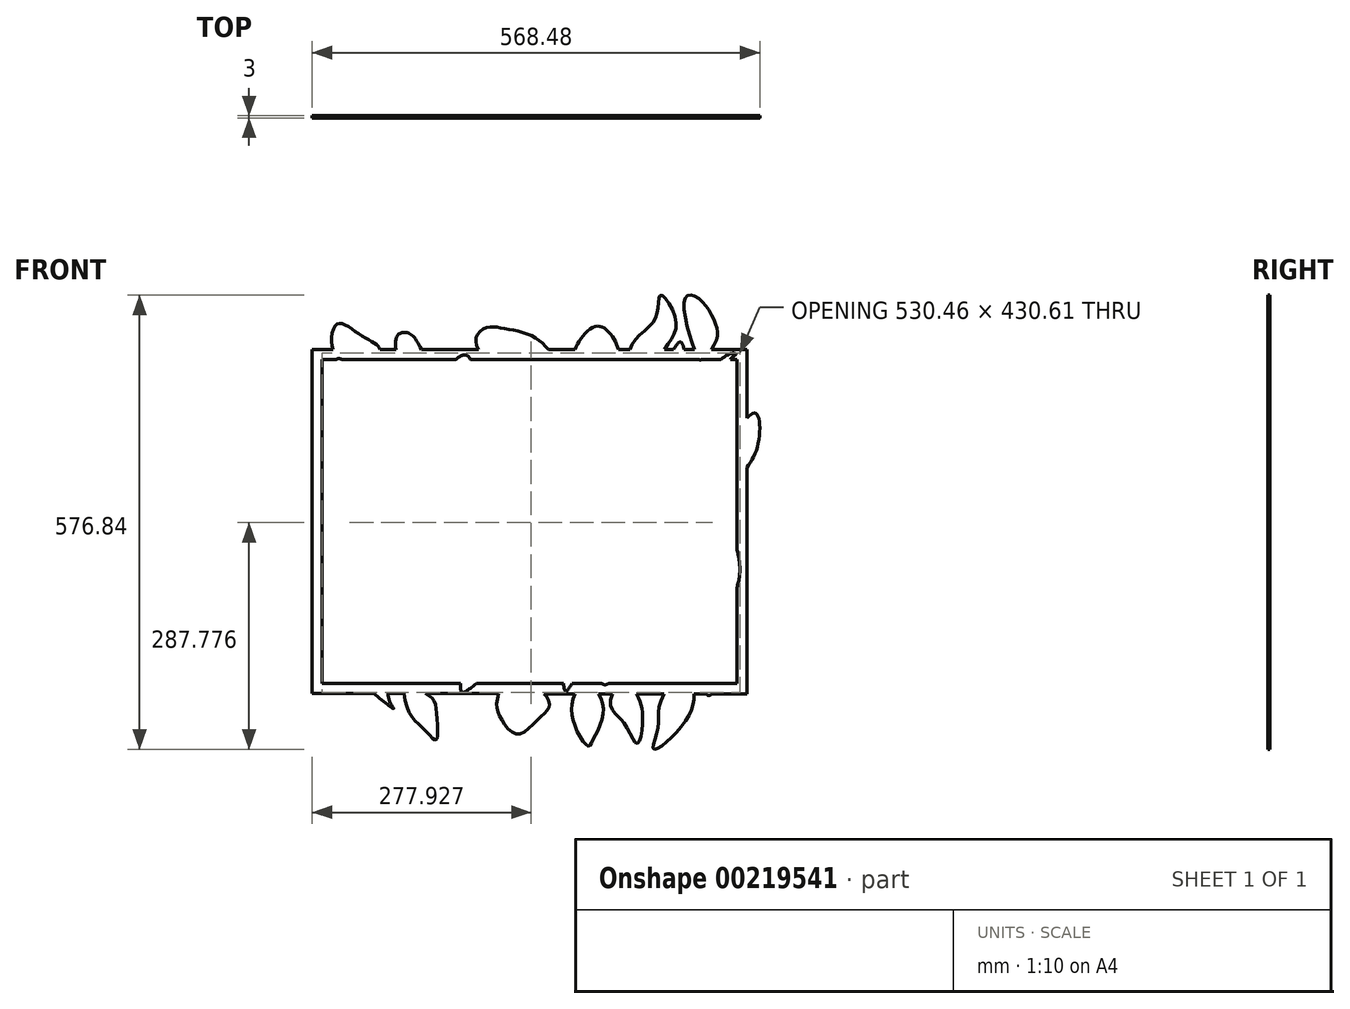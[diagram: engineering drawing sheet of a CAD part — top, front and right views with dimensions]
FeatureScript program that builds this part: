
annotation { "Feature Type Name" : "Feature", "Feature Type Description" : "" }
export const myFeature = defineFeature(function(context is Context, id is Id, definition is map)
    precondition{}
    {
        {
            var Q0;
            Q0=qCreatedBy(makeId("Front.planeOp"),FACE);
            var sketch = newSketch(context, id + "F0", { "sketchPlane" : qUnion([Q0])});
            skFitSpline(sketch, "E0", {"points": [v(11.73, -257.24) * mm, v(27.73, -248.2) * mm, v(55.77, -225.45) * mm, v(81.09, -202.2) * mm, v(78.35, -181.47) * mm, v(59.49, -185.65) * mm, v(38.93, -186.47) * mm, v(24.9, -183.93) * mm, v(6.94, -198.84) * mm, v(9.55, -234.86) * mm, v(11.73, -257.24) * mm]});
            skFitSpline(sketch, "E1", {"points": [v(0, -177.41) * mm, v(17.54, -147.8) * mm, v(17.54, -118.2) * mm, v(0, -92.72) * mm, v(-24.4, -74.63) * mm, v(-40.84, -98.47) * mm, v(-19.46, -134.65) * mm, v(0, -177.41) * mm]});
            skFitSpline(sketch, "E2", {"points": [v(29.05, -165.08) * mm, v(38.92, -149.45) * mm, v(38.92, -117.39) * mm, v(60.3, -90.25) * mm, v(71.81, -103.4) * mm, v(67.7, -117.39) * mm, v(70.17, -144.52) * mm, v(74.28, -157.68) * mm, v(53.2, -171.85) * mm, v(31.03, -176.91) * mm, v(29.05, -165.08) * mm]});
            skFitSpline(sketch, "E3", {"points": [v(82.53, -310.53) * mm, v(111.54, -288.78) * mm, v(122.93, -273.24) * mm, v(112.57, -257.7) * mm, v(99.1, -257.7) * mm, v(83.56, -229.72) * mm, v(74.24, -229.72) * mm, v(56.63, -266.22) * mm, v(60.77, -289.81) * mm, v(82.53, -310.53) * mm]});
            skFitSpline(sketch, "E4", {"points": [v(169.55, -244.23) * mm, v(181.98, -253.55) * mm, v(191.3, -284.63) * mm, v(177.84, -318.82) * mm, v(172.66, -326.07) * mm, v(156.08, -302.24) * mm, v(152.98, -266.22) * mm, v(169.55, -244.23) * mm]});
            skFitSpline(sketch, "E5", {"points": [v(-59.4, -240.08) * mm, v(-43.86, -252.52) * mm, v(-25.21, -266.22) * mm, v(-20.03, -289.81) * mm, v(-21.07, -317.78) * mm, v(-36.61, -304.32) * mm, v(-57.33, -278.42) * mm, v(-59.4, -240.08) * mm]});
            skFitSpline(sketch, "E6", {"points": [v(-49.04, -177.92) * mm, v(-29.36, -194.5) * mm, v(-15.9, -222.47) * mm, v(-14.85, -241.12) * mm, v(-36.61, -226.62) * mm, v(-58.37, -204.86) * mm, v(-49.04, -177.92) * mm]});
            skFitSpline(sketch, "E7", {"points": [v(-111.2, -188.28) * mm, v(-120.53, -201.75) * mm, v(-123.63, -219.36) * mm, v(-117.42, -240.08) * mm, v(-91.52, -266.22) * mm, v(-74.94, -278.42) * mm, v(-81.16, -266.22) * mm, v(-78.05, -229.72) * mm, v(-93.6, -194.5) * mm, v(-111.2, -188.28) * mm]});
            skFitSpline(sketch, "E8", {"points": [v(-154.71, -117.84) * mm, v(-132.96, -144.77) * mm, v(-110.17, -165.5) * mm, v(-101.88, -132.34) * mm, v(-116.38, -110.58) * mm, v(-153.68, -96.08) * mm, v(-154.71, -117.84) * mm]});
            skFitSpline(sketch, "E9", {"points": [v(-154.71, -159.28) * mm, v(-154.71, -203.82) * mm, v(-148.5, -212.11) * mm, v(-129.85, -187.25) * mm, v(-132.96, -163.42) * mm, v(-154.71, -159.28) * mm]});
            skFitSpline(sketch, "E10", {"points": [v(-94.63, -103.33) * mm, v(-80.12, -131.3) * mm, v(-35.57, -167.56) * mm, v(-36.61, -148.92) * mm, v(-75.98, -108.51) * mm, v(-83.23, -92.97) * mm, v(-94.63, -103.33) * mm]});
            skFitSpline(sketch, "E11", {"points": [v(88.68, -107.63) * mm, v(102.6, -122.28) * mm, v(129.7, -150.85) * mm, v(142.16, -184.55) * mm, v(132.63, -195.54) * mm, v(124.57, -186.01) * mm, v(104.8, -162.57) * mm, v(86.48, -142.06) * mm, v(88.68, -107.63) * mm]});
            skFitSpline(sketch, "E12", {"points": [v(89.41, -175.76) * mm, v(92.34, -194.8) * mm, v(104.06, -228.5) * mm, v(122.38, -240.08) * mm, v(128.97, -227.77) * mm, v(116.52, -195.54) * mm, v(89.41, -175.76) * mm]});
            skFitSpline(sketch, "E13", {"points": [v(150.95, -187.48) * mm, v(145.09, -201.75) * mm, v(142.16, -221.9) * mm, v(140.69, -244.23) * mm, v(143.62, -256.34) * mm, v(152.98, -244.23) * mm, v(169.55, -221.9) * mm, v(169.55, -191.14) * mm, v(150.95, -187.48) * mm]});
            skFitSpline(sketch, "E14", {"points": [v(130.43, -122.28) * mm, v(152.98, -130.34) * mm, v(175.12, -141.33) * mm, v(185.38, -145.72) * mm, v(194.17, -156.7) * mm, v(161.2, -171.36) * mm, v(130.43, -122.28) * mm]});
            skFitSpline(sketch, "E15", {"points": [v(24.78, -46.13) * mm, v(45.35, -76.51) * mm, v(42.07, -84.93) * mm, v(36, -98.95) * mm, v(27.12, -106.9) * mm, v(11.7, -68.1) * mm, v(24.78, -46.13) * mm]});
            skFitSpline(sketch, "E16", {"points": [v(-151.44, -40.05) * mm, v(-139.28, -50.8) * mm, v(-115.91, -70.44) * mm, v(-98.15, -86.33) * mm, v(-101.42, -91.94) * mm, v(-121.06, -89.13) * mm, v(-146.3, -72.3) * mm, v(-151.44, -40.05) * mm]});
            skFitSpline(sketch, "E17", {"points": [v(-150.5, -11.07) * mm, v(-128.53, -38.65) * mm, v(-93.94, -68.1) * mm, v(-61.7, -97.08) * mm, v(-52.34, -96.14) * mm, v(-64.5, -62.49) * mm, v(-113.58, -21.36) * mm, v(-144.9, -6.4) * mm, v(-150.5, -11.07) * mm]});
            skFitSpline(sketch, "E18", {"points": [v(80.4, -74.18) * mm, v(88.82, -83.06) * mm, v(102.37, -91.94) * mm, v(115.93, -93.8) * mm, v(112.65, -75.11) * mm, v(103.3, -46.6) * mm, v(91.62, -35.38) * mm, v(81.34, -52.67) * mm, v(80.4, -74.18) * mm]});
            skFitSpline(sketch, "E19", {"points": [v(64.98, -59.69) * mm, v(65.45, -50.34) * mm, v(74.33, -31.64) * mm, v(82.74, -18.55) * mm, v(81.34, -6.4) * mm, v(68.25, 41.28) * mm, v(58.43, 28.66) * mm, v(46.75, -15.75) * mm, v(56.1, -53.6) * mm, v(64.98, -59.69) * mm]});
            skFitSpline(sketch, "E20", {"points": [v(166.35, -50.07) * mm, v(167.92, -63.71) * mm, v(172.12, -77.88) * mm, v(177.9, -98.87) * mm, v(192.06, -110.58) * mm, v(204.12, -91.94) * mm, v(185.76, -51.65) * mm, v(171.6, -44.83) * mm, v(166.35, -50.07) * mm]});
            skFitSpline(sketch, "E21", {"points": [v(93.94, -11.25) * mm, v(101.3, -26.99) * mm, v(118.08, -47.45) * mm, v(142.74, -59.52) * mm, v(152.98, -58.47) * mm, v(145.36, -27.51) * mm, v(113.88, 8.69) * mm, v(101.81, 7.64) * mm, v(93.94, -11.25) * mm]});
            skFitSpline(sketch, "E22", {"points": [v(168.97, -3.38) * mm, v(169.5, -12.82) * mm, v(182.61, -28.04) * mm, v(193.63, -39.05) * mm, v(207.8, -55.32) * mm, v(207.8, -7.57) * mm, v(181.56, 27.05) * mm, v(168.97, -3.38) * mm]});
            skFitSpline(sketch, "E23", {"points": [v(119.13, 31.25) * mm, v(129.1, 20.23) * mm, v(148.5, -3.9) * mm, v(159.53, 0) * mm, v(166.35, 32.3) * mm, v(135.4, 51.19) * mm, v(120.7, 43.84) * mm, v(119.13, 31.25) * mm]});
            skFitSpline(sketch, "E24", {"points": [v(96.04, 86.34) * mm, v(114.4, 65.88) * mm, v(107.06, 41.22) * mm, v(88.68, 37.55) * mm, v(74.28, 63.25) * mm, v(81.88, 77.94) * mm, v(96.04, 86.34) * mm]});
            skFitSpline(sketch, "E25", {"points": [v(41.48, 32.3) * mm, v(48.3, 38.6) * mm, v(60.9, 64.3) * mm, v(62.47, 90.54) * mm, v(48.82, 118.34) * mm, v(25.74, 82.14) * mm, v(22.07, 59.06) * mm, v(41.48, 32.3) * mm]});
            skFitSpline(sketch, "E26", {"points": [v(-151.6, 11.31) * mm, v(-141.1, 8.69) * mm, v(-116.38, 0) * mm, v(-94.13, -19.12) * mm, v(-84.96, -23.84) * mm, v(-81.82, -9.67) * mm, v(-94.13, 0) * mm, v(-113.05, 9.74) * mm, v(-137.96, 26.53) * mm, v(-151.6, 42.27) * mm, v(-151.6, 11.31) * mm]});
            skFitSpline(sketch, "E27", {"points": [v(-81.82, 19.18) * mm, v(-73.95, 10.79) * mm, v(-68.18, -4.43) * mm, v(-68.7, -19.12) * mm, v(-71.85, -24.89) * mm, v(-70.8, -31.7) * mm, v(-58.2, -47.45) * mm, v(-50.34, -65.29) * mm, v(-45.1, -76.3) * mm, v(-36.61, -69.48) * mm, v(-28.83, -51.12) * mm, v(-36.61, -30.66) * mm, v(-36.61, -7.05) * mm, v(-56.63, 27.05) * mm, v(-78.67, 34.4) * mm, v(-81.82, 19.18) * mm]});
            skFitSpline(sketch, "E28", {"points": [v(-9.94, 10.79) * mm, v(-2.6, -2.33) * mm, v(16.3, -25.94) * mm, v(3.7, -52.17) * mm, v(-21.48, -34.86) * mm, v(-24.63, -4.43) * mm, v(-9.94, 10.79) * mm]});
            skFitSpline(sketch, "E29", {"points": [v(2.65, 26) * mm, v(16.82, -0.23) * mm, v(31.76, -19.64) * mm, v(36.23, 0) * mm, v(21.54, 40.7) * mm, v(15.25, 51.19) * mm, v(2.65, 26) * mm]});
            skFitSpline(sketch, "E30", {"points": [v(-151.6, 91.06) * mm, v(-151.6, 64.83) * mm, v(-131.66, 42.8) * mm, v(-105.95, 24.95) * mm, v(-94.13, 20.76) * mm, v(-101.42, 61.16) * mm, v(-127.99, 82.14) * mm, v(-151.6, 91.06) * mm]});
            skFitSpline(sketch, "E31", {"points": [v(-13.61, 113.1) * mm, v(-18.86, 85.81) * mm, v(-15.7, 59.58) * mm, v(-6.27, 37.55) * mm, v(6.85, 67.98) * mm, v(6.33, 87.91) * mm, v(-6.8, 112.57) * mm, v(-13.61, 113.1) * mm]});
            skFitSpline(sketch, "E32", {"points": [v(-71.5, 193.12) * mm, v(-71.65, 165.2) * mm, v(-75.95, 144.76) * mm, v(-67.05, 121.41) * mm, v(-52.6, 110.3) * mm, v(-40.93, 101.96) * mm, v(-37.04, 85.84) * mm, v(-32.03, 77.5) * mm, v(-26.47, 93.07) * mm, v(-26.47, 139.76) * mm, v(-39.81, 178.11) * mm, v(-50.93, 195.34) * mm, v(-62.05, 199.8) * mm, v(-71.5, 193.12) * mm]});
            skFitSpline(sketch, "E33", {"points": [v(102.03, 110.75) * mm, v(103.7, 106.17) * mm, v(114.52, 84.93) * mm, v(132.43, 64.53) * mm, v(150.75, 60.36) * mm, v(175.73, 53.7) * mm, v(191.14, 38.71) * mm, v(200.18, 34.3) * mm, v(189.15, 64.74) * mm, v(181.65, 89.45) * mm, v(178.56, 96.06) * mm, v(154.3, 120.77) * mm, v(126.06, 129.15) * mm, v(108.85, 122.54) * mm, v(102.03, 110.75) * mm]});
            skFitSpline(sketch, "E34", {"points": [v(91.65, 129.6) * mm, v(109.74, 143.27) * mm, v(139.3, 146.36) * mm, v(133.12, 160.04) * mm, v(118.12, 182.1) * mm, v(92.97, 198.42) * mm, v(62.97, 205.04) * mm, v(44, 205.92) * mm, v(29.88, 192.68) * mm, v(40.03, 166.21) * mm, v(70.03, 137.1) * mm, v(91.65, 129.6) * mm]});
            skFitSpline(sketch, "E35", {"points": [v(-110.26, 133.63) * mm, v(-102.48, 121.4) * mm, v(-79.13, 106.4) * mm, v(-70.24, 101.4) * mm, v(-91.92, 93.06) * mm, v(-106.37, 93.06) * mm, v(-121.93, 106.95) * mm, v(-110.26, 133.63) * mm]});
            skFitSpline(sketch, "E36", {"points": [v(-149.17, 110.29) * mm, v(-148, 165.24) * mm, v(-125.83, 146.42) * mm, v(-130.83, 115.29) * mm, v(-149.17, 110.29) * mm]});
            skFitSpline(sketch, "E37", {"points": [v(-147.5, 209.79) * mm, v(-121.93, 199.78) * mm, v(-95.8, 183.1) * mm, v(-90.25, 170.88) * mm, v(-88.03, 134.19) * mm, v(-109.15, 151.42) * mm, v(-129.72, 169.2) * mm, v(-150.84, 175.32) * mm, v(-147.5, 209.79) * mm]});
            skFitSpline(sketch, "E38", {"points": [v(-96.5, 70.6) * mm, v(-92.52, 77.94) * mm, v(-61.43, 87.91) * mm, v(-44.24, 77.94) * mm, v(-34.97, 52.75) * mm, v(-52.83, 46.14) * mm, v(-79.3, 48.78) * mm, v(-96.5, 70.6) * mm]});
            skFitSpline(sketch, "E39", {"points": [v(15.96, 171.07) * mm, v(28.53, 153.22) * mm, v(38.45, 132.73) * mm, v(17.94, 101.66) * mm, v(6.33, 106.3) * mm, v(-9.18, 142.65) * mm, v(15.96, 171.07) * mm]});
            skFitSpline(sketch, "E40", {"points": [v(155.02, 160.04) * mm, v(163.93, 142.37) * mm, v(183.6, 120.1) * mm, v(196.6, 120.85) * mm, v(211.08, 153.22) * mm, v(207.74, 185.77) * mm, v(183.24, 207.56) * mm, v(155.02, 177.24) * mm, v(155.02, 160.04) * mm]});
            skFitSpline(sketch, "E41", {"points": [v(255, -329.08) * mm, v(260.78, -302.84) * mm, v(263.4, -270.84) * mm, v(294.9, -233.59) * mm, v(305.93, -253.53) * mm, v(300.68, -285.53) * mm, v(267.08, -324.36) * mm, v(255, -329.08) * mm]});
            skFitSpline(sketch, "E42", {"points": [v(298.43, -77.68) * mm, v(285.68, -90.01) * mm, v(268, -110.57) * mm, v(256.5, -133.6) * mm, v(256.5, -162.78) * mm, v(265.54, -173.88) * mm, v(277.87, -168.54) * mm, v(281.57, -145.93) * mm, v(301.72, -117.97) * mm, v(309.12, -104.4) * mm, v(298.43, -77.68) * mm]});
            skFitSpline(sketch, "E43", {"points": [v(342, -56.7) * mm, v(331.73, -70.69) * mm, v(323.5, -85.49) * mm, v(321.86, -102.76) * mm, v(348.59, -143.87) * mm, v(354.75, -139.35) * mm, v(364.62, -105.22) * mm, v(353.52, -61.23) * mm, v(342, -56.7) * mm]});
            skFitSpline(sketch, "E44", {"points": [v(236.76, -58.35) * mm, v(233.06, -68.63) * mm, v(238.81, -87.54) * mm, v(255.67, -94.12) * mm, v(280.75, -74.39) * mm, v(295.96, -58.77) * mm, v(294.32, -30.4) * mm, v(292.26, -22.17) * mm, v(284.04, -5.73) * mm, v(278.28, -9.43) * mm, v(267.18, -35.33) * mm, v(236.76, -58.35) * mm]});
            skFitSpline(sketch, "E45", {"points": [v(229.3, -29.29) * mm, v(237.35, -17.2) * mm, v(247.97, 13.2) * mm, v(253.1, 37) * mm, v(280.94, 45.07) * mm, v(290.46, 41.77) * mm, v(289.36, 30.42) * mm, v(278, 20.16) * mm, v(254.56, -31.12) * mm, v(231.49, -39.18) * mm, v(229.3, -29.29) * mm]});
            skFitSpline(sketch, "E46", {"points": [v(199.4, 98.34) * mm, v(207.08, 73.64) * mm, v(221.35, 5.6) * mm, v(231.23, 12.73) * mm, v(244.4, 53.34) * mm, v(247.7, 102.18) * mm, v(222.45, 137.3) * mm, v(208.73, 117) * mm, v(199.4, 98.34) * mm]});
            skFitSpline(sketch, "E47", {"points": [v(264.16, 61.57) * mm, v(284.46, 89.01) * mm, v(332.2, 110.96) * mm, v(343.74, 112.06) * mm, v(351.41, 93.95) * mm, v(313.55, 55.53) * mm, v(295.99, 64.86) * mm, v(264.16, 61.57) * mm]});
            skFitSpline(sketch, "E48", {"points": [v(307.51, -10.32) * mm, v(317.39, 0) * mm, v(337.15, 29.74) * mm, v(343.74, 52.24) * mm, v(325.62, 46.2) * mm, v(305.86, 21.5) * mm, v(307.51, -10.32) * mm]});
            skFitSpline(sketch, "E49", {"points": [v(348.67, 10.53) * mm, v(350.32, 30.29) * mm, v(357.45, 63.22) * mm, v(383.8, 97.24) * mm, v(388.18, 59.37) * mm, v(364.04, 17.67) * mm, v(348.67, 10.53) * mm]});
            skFitSpline(sketch, "E50", {"points": [v(245.82, 147.4) * mm, v(256.57, 158.64) * mm, v(274.66, 186.5) * mm, v(283.95, 210.47) * mm, v(270.75, 242.25) * mm, v(263.42, 246.65) * mm, v(260.97, 232.96) * mm, v(255.1, 213.4) * mm, v(233.6, 192.38) * mm, v(225.77, 169.4) * mm, v(245.82, 147.4) * mm]});
            skFitSpline(sketch, "E51", {"points": [v(259.5, 98.5) * mm, v(254.62, 118.55) * mm, v(270.26, 159.62) * mm, v(289.33, 187.49) * mm, v(295.2, 172.82) * mm, v(297.64, 143.97) * mm, v(259.5, 98.5) * mm]});
            skFitSpline(sketch, "E52", {"points": [v(301.55, 116.6) * mm, v(316.71, 117.08) * mm, v(343.74, 136.64) * mm, v(352.4, 165) * mm, v(359.74, 171.84) * mm, v(349.96, 171.35) * mm, v(301.55, 116.6) * mm]});
            skFitSpline(sketch, "E53", {"points": [v(295.2, 243.14) * mm, v(309.38, 171.35) * mm, v(315.73, 165) * mm, v(334.8, 189.44) * mm, v(332.85, 213.4) * mm, v(311.82, 243.14) * mm, v(295.2, 243.14) * mm]});
            skFitSpline(sketch, "E54", {"points": [v(312.23, -193.43) * mm, v(318.23, -198.97) * mm, v(328.39, -208.2) * mm, v(335.77, -226.66) * mm, v(340.38, -239.12) * mm, v(334.85, -252.5) * mm, v(325.62, -261.73) * mm, v(320.54, -256.2) * mm, v(310.85, -231.27) * mm, v(303, -219.74) * mm, v(305.77, -196.2) * mm, v(312.23, -193.43) * mm]});
            skFitSpline(sketch, "E55", {"points": [v(263.78, -240.5) * mm, v(276.24, -231.73) * mm, v(288.7, -209.58) * mm, v(290.54, -178.2) * mm, v(287.31, -172.66) * mm, v(271.16, -190.66) * mm, v(262.4, -228.5) * mm, v(263.78, -240.5) * mm]});
            skFitSpline(sketch, "E56", {"points": [v(222.24, -241.42) * mm, v(232.4, -257.12) * mm, v(238.86, -271.88) * mm, v(241.16, -286.65) * mm, v(237.47, -318.5) * mm, v(232.86, -322.18) * mm, v(219.48, -298.65) * mm, v(206.55, -285.27) * mm, v(201.02, -264.5) * mm, v(222.24, -241.42) * mm]});
            skFitSpline(sketch, "E57", {"points": [v(204.7, -163.9) * mm, v(209.78, -181.43) * mm, v(225.01, -222.04) * mm, v(241.63, -236.8) * mm, v(240.7, -205.9) * mm, v(224.1, -171.74) * mm, v(209.32, -157.9) * mm, v(204.7, -163.9) * mm]});
            skFitSpline(sketch, "E58", {"points": [v(185.33, -176.82) * mm, v(178.86, -187.9) * mm, v(179.33, -222.97) * mm, v(192.7, -247.89) * mm, v(207.48, -225.73) * mm, v(192.7, -176.36) * mm, v(185.33, -176.82) * mm]});
            skFitSpline(sketch, "E59", {"points": [v(126.44, -74.69) * mm, v(129.73, -100.18) * mm, v(160.98, -110.46) * mm, v(153.57, -85.79) * mm, v(137.13, -74.28) * mm, v(126.44, -74.69) * mm]});
            skFitSpline(sketch, "E60", {"points": [v(214.18, -126.31) * mm, v(220.76, -109.85) * mm, v(237.77, -142.78) * mm, v(224.05, -134.54) * mm, v(214.18, -126.31) * mm]});
            skLineSegment(sketch, "E61.bottom", {"start": v(-165.74, 165.2) * mm, "end": v(-148.06, 165.2) * mm});
            skLineSegment(sketch, "E61.left", {"start": v(-165.74, 165.2) * mm, "end": v(-165.74, -246.14) * mm});
            skLineSegment(sketch, "E61.right", {"start": v(360.98, 165.2) * mm, "end": v(360.98, 70.9) * mm});
            skFitSpline(sketch, "E62", {"points": [v(-83.11, -167.1) * mm, v(-88.3, -178.51) * mm, v(-69.63, -192.51) * mm, v(-66, -170.22) * mm, v(-71.7, -162.44) * mm, v(-83.11, -167.1) * mm]});
            skFitSpline(sketch, "E63", {"points": [v(320.24, -182.17) * mm, v(300.45, -157.24) * mm, v(305.58, -127.9) * mm, v(327.58, -136.7) * mm, v(351.04, -196.83) * mm, v(353.24, -222.5) * mm, v(328.39, -192.43) * mm, v(320.24, -182.17) * mm]});
            skFitSpline(sketch, "E64", {"points": [v(347.37, -5.46) * mm, v(328.39, -9.13) * mm, v(304.11, -39.19) * mm, v(319.51, -67.05) * mm, v(347.37, -5.46) * mm]});
            skLineSegment(sketch, "E65.trimOffspring", {"start": v(-140.6, 165.2) * mm, "end": v(-121.86, 165.2) * mm});
            skLineSegment(sketch, "E66.trimOffspring", {"start": v(-89.08, 165.2) * mm, "end": v(-71.65, 165.2) * mm});
            skLineSegment(sketch, "E67.trimOffspring", {"start": v(-34.07, 165.2) * mm, "end": v(3.84, 165.2) * mm});
            skLineSegment(sketch, "E68.trimOffspring", {"start": v(22.65, 165.2) * mm, "end": v(40.8, 165.2) * mm});
            skLineSegment(sketch, "E69.trimOffspring", {"start": v(129.83, 165.2) * mm, "end": v(153.65, 165.2) * mm});
            skLineSegment(sketch, "E70.trimOffspring", {"start": v(260.52, 165.2) * mm, "end": v(273.17, 165.2) * mm});
            skLineSegment(sketch, "E71.trimOffspring", {"start": v(316.2, 165.2) * mm, "end": v(340.61, 165.2) * mm});
            skLineSegment(sketch, "E72.trimOffspring", {"start": v(352.55, 165.2) * mm, "end": v(360.98, 165.2) * mm});
            skLineSegment(sketch, "E73", {"start": v(212.33, 165.2) * mm, "end": v(227.35, 165.2) * mm});
            skLineSegment(sketch, "E74.trimOffspring", {"start": v(-79.99, -246.13) * mm, "end": v(-61.72, -246.13) * mm});
            skLineSegment(sketch, "E75.trimOffspring", {"start": v(91.64, -246.13) * mm, "end": v(140.79, -246.14) * mm});
            skLineSegment(sketch, "E76.trimOffspring", {"start": v(30.2, -246.13) * mm, "end": v(63.46, -246.13) * mm});
            skLineSegment(sketch, "E77.trimOffspring", {"start": v(151.65, -246.14) * mm, "end": v(165.54, -246.14) * mm});
            skLineSegment(sketch, "E78.trimOffspring", {"start": v(175.74, -246.14) * mm, "end": v(189.23, -246.14) * mm});
            skLineSegment(sketch, "E79", {"start": v(-165.74, -246.14) * mm, "end": v(-113.02, -246.14) * mm});
            skLineSegment(sketch, "E80.trimOffspring", {"start": v(338.6, -246.14) * mm, "end": v(360.98, -246.14) * mm});
            skLineSegment(sketch, "E81.trimOffspring", {"start": v(304.49, -246.14) * mm, "end": v(316.96, -246.14) * mm});
            skLineSegment(sketch, "E82.trimOffspring", {"start": v(227.87, -246.14) * mm, "end": v(277.71, -246.14) * mm});
            skLineSegment(sketch, "E83.trimOffspring", {"start": v(198.08, -246.14) * mm, "end": v(212.76, -246.14) * mm});
            skLineSegment(sketch, "E84.trimOffspring", {"start": v(-50.37, -246.13) * mm, "end": v(9.8, -246.13) * mm});
            skLineSegment(sketch, "E85.trimOffspring", {"start": v(360.98, -124.64) * mm, "end": v(360.98, -246.14) * mm});
            skLineSegment(sketch, "E86.trimOffspring", {"start": v(360.98, 15.19) * mm, "end": v(360.98, -76.53) * mm});
            skLineSegment(sketch, "E87.trimOffspring", {"start": v(297.57, 165.2) * mm, "end": v(312.94, 165.2) * mm});
            skFitSpline(sketch, "E88", {"points": [v(68.6, 116.9) * mm, v(76.05, 90.27) * mm, v(90.43, 101.46) * mm, v(78.18, 111.57) * mm, v(68.6, 116.9) * mm]});
            skPoint(sketch, "E89.orphan", {"position": v(367.33, -253.53) * mm});
            skPoint(sketch, "E90.orphan", {"position": v(367.33, -246.14) * mm});
            skLineSegment(sketch, "E91", {"start": v(-121.86, 165.2) * mm, "end": v(-89.08, 165.2) * mm});
            skLineSegment(sketch, "E92", {"start": v(-71.65, 165.2) * mm, "end": v(-34.07, 165.2) * mm});
            skLineSegment(sketch, "E93", {"start": v(3.84, 165.2) * mm, "end": v(22.65, 165.2) * mm});
            skLineSegment(sketch, "E94", {"start": v(40.8, 165.2) * mm, "end": v(129.83, 165.2) * mm});
            skLineSegment(sketch, "E95", {"start": v(153.65, 165.2) * mm, "end": v(212.33, 165.2) * mm});
            skLineSegment(sketch, "E96", {"start": v(227.35, 165.2) * mm, "end": v(260.52, 165.2) * mm});
            skLineSegment(sketch, "E97", {"start": v(273.17, 165.2) * mm, "end": v(297.57, 165.2) * mm});
            skLineSegment(sketch, "E98", {"start": v(340.61, 165.2) * mm, "end": v(352.4, 165) * mm});
            skLineSegment(sketch, "E99", {"start": v(360.98, 70.9) * mm, "end": v(360.98, 15.19) * mm});
            skLineSegment(sketch, "E100", {"start": v(360.98, -76.53) * mm, "end": v(360.98, -124.64) * mm});
            skLineSegment(sketch, "E101", {"start": v(338.6, -246.14) * mm, "end": v(316.96, -246.14) * mm});
            skLineSegment(sketch, "E102", {"start": v(304.49, -246.14) * mm, "end": v(277.71, -246.14) * mm});
            skLineSegment(sketch, "E103", {"start": v(227.87, -246.14) * mm, "end": v(212.76, -246.14) * mm});
            skLineSegment(sketch, "E104", {"start": v(198.08, -246.14) * mm, "end": v(189.23, -246.14) * mm});
            skLineSegment(sketch, "E105", {"start": v(175.74, -246.14) * mm, "end": v(165.54, -246.14) * mm});
            skLineSegment(sketch, "E106", {"start": v(151.65, -246.14) * mm, "end": v(140.79, -246.14) * mm});
            skLineSegment(sketch, "E107", {"start": v(91.64, -246.13) * mm, "end": v(63.46, -246.13) * mm});
            skLineSegment(sketch, "E108", {"start": v(30.2, -246.13) * mm, "end": v(9.8, -246.13) * mm});
            skLineSegment(sketch, "E109", {"start": v(-50.37, -246.13) * mm, "end": v(-61.72, -246.13) * mm});
            skLineSegment(sketch, "E110", {"start": v(-79.99, -246.13) * mm, "end": v(-113.02, -246.14) * mm});
            skLineSegment(sketch, "E111", {"start": v(-148.06, 165.2) * mm, "end": v(-140.6, 165.2) * mm});
            skLineSegment(sketch, "E112.0", {"start": v(-178.44, 177.9) * mm, "end": v(-178.44, -258.7) * mm});
            skLineSegment(sketch, "E113.0", {"start": v(-178.44, 177.9) * mm, "end": v(373.68, 177.9) * mm});
            skLineSegment(sketch, "E114.0", {"start": v(373.68, 177.9) * mm, "end": v(373.68, -259.89) * mm});
            skLineSegment(sketch, "E115.0", {"start": v(-178.44, -258.7) * mm, "end": v(373.68, -259.89) * mm});
            skSolve(sketch);
        }
        {
            var Q0;
            Q0 = qSketchRegion(id + "F0", true);
            var Q1;
            Q1=makeQuery(id+"F0.imprint","IMPRINT",FACE,{"disambiguationData":[TD([[makeQuery(id+"F0.imprint","IMPRINT",EDGE,{"derivedFrom":sQuery(id+"F0.wireOp",EDGE,"E0")}),-1.0]])]});
            extrude(context, id + "F1", {"entities" : qUnion([Q0, Q1]), "depth" : 3 * mm});
        }
    });
